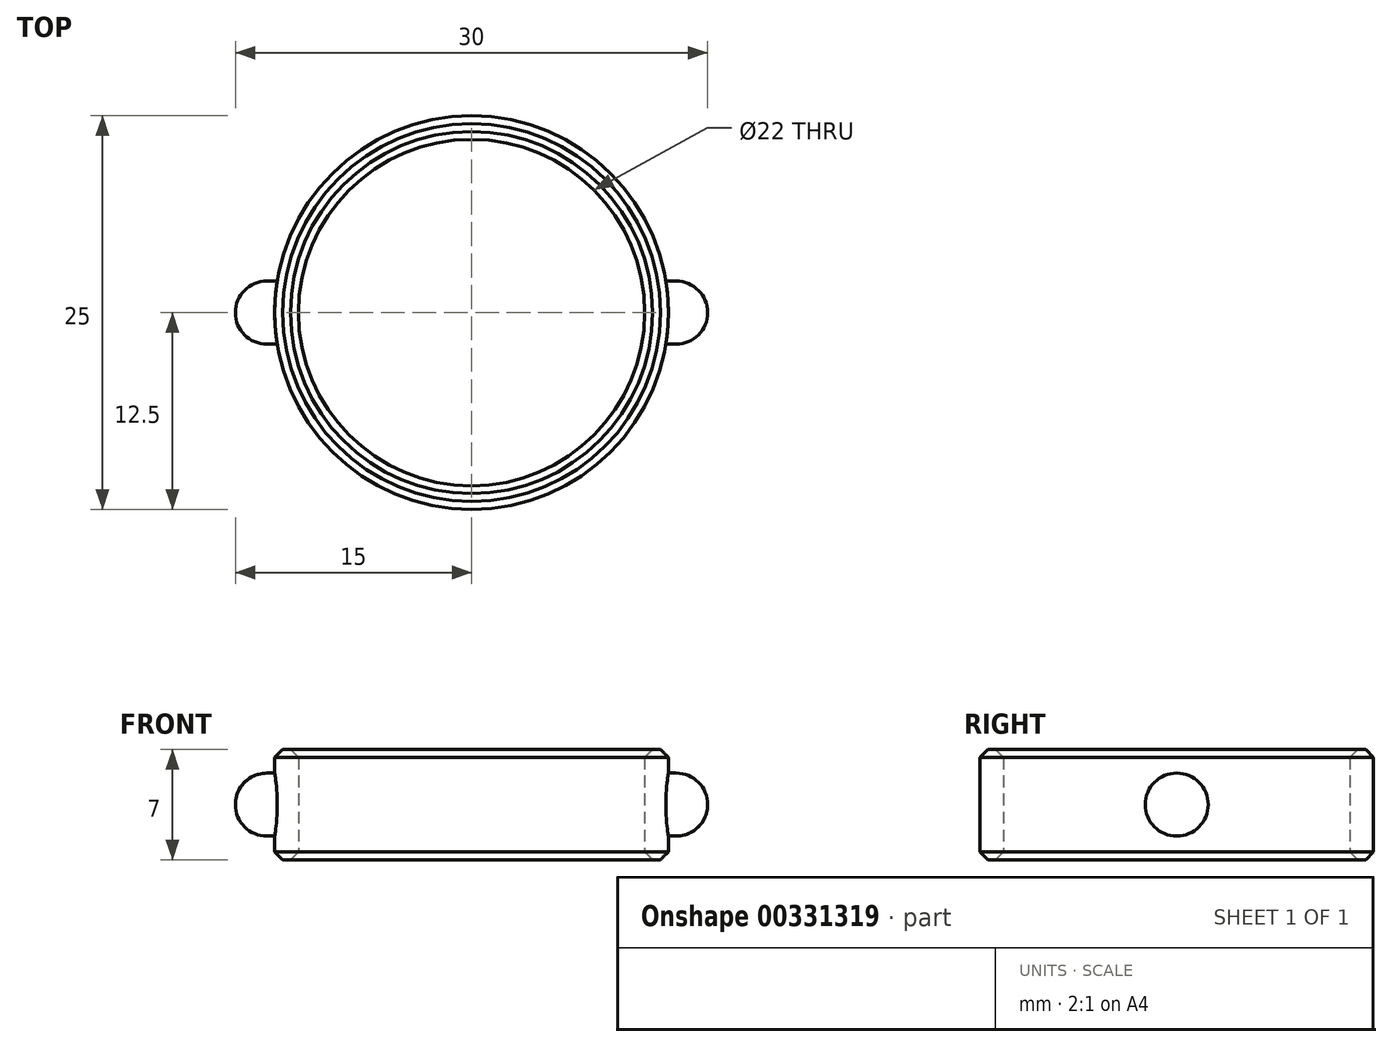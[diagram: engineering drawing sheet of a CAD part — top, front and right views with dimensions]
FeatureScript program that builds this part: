
annotation { "Feature Type Name" : "Feature", "Feature Type Description" : "" }
export const myFeature = defineFeature(function(context is Context, id is Id, definition is map)
    precondition{}
    {
        {
            var Q0;
            Q0=qCreatedBy(makeId("Top.planeOp"),FACE);
            var sketch = newSketch(context, id + "F0", { "sketchPlane" : qUnion([Q0])});
            skCircle(sketch, "E0", {"center": v(0, 0) * mm, "radius": 11 * mm});
            skCircle(sketch, "E1", {"center": v(0, 0) * mm, "radius": 12.5 * mm});
            skSolve(sketch);
        }
        {
            var Q0;
            Q0=makeQuery(id+"F0.imprint","IMPRINT",FACE,{"disambiguationData":[TD([[makeQuery(id+"F0.imprint","IMPRINT",EDGE,{"derivedFrom":sQuery(id+"F0.wireOp",EDGE,"E0")}),-1.0]])]});
            extrude(context, id + "F1", {"entities" : qUnion([Q0]), "depth" : 7 * mm});
        }
        {
            var Q0;
            Q0=makeQuery(id+"F1.opExtrude","CAP_EDGE",EDGE,{"disambiguationData":[OSD([sQuery(id+"F0.wireOp",EDGE,"E0")])],"isStart":false});
            var Q1;
            Q1=makeQuery(id+"F1.opExtrude","CAP_EDGE",EDGE,{"disambiguationData":[OSD([sQuery(id+"F0.wireOp",EDGE,"E1")])],"isStart":false});
            var Q2;
            Q2=makeQuery(id+"F1.opExtrude","CAP_EDGE",EDGE,{"disambiguationData":[OSD([sQuery(id+"F0.wireOp",EDGE,"E1")])],"isStart":true});
            var Q3;
            Q3=makeQuery(id+"F1.opExtrude","CAP_EDGE",EDGE,{"disambiguationData":[OSD([sQuery(id+"F0.wireOp",EDGE,"E0")])],"isStart":true});
            chamfer(context, id + "F2", {"entities" : qUnion([Q0, Q1, Q2, Q3]), "width" : .5 * mm, "tangentPropagation" : true});
        }
        {
            var Q0;
            Q0=qCreatedBy(makeId("Right.planeOp"),FACE);
            cPlane(context, id + "F3", {"entities" : qUnion([Q0]), "cplaneType" : CPlaneType.OFFSET, "offset" : 11 * mm, "width" : 150 * mm, "height" : 150 * mm});
        }
        {
            var Q0;
            Q0=qCreatedBy(id+"F3.planeOp",FACE);
            var sketch = newSketch(context, id + "F4", { "sketchPlane" : qUnion([Q0])});
            skCircle(sketch, "E2", {"center": v(0, 3.5) * mm, "radius": 2 * mm});
            skLineSegment(sketch, "E3", {"start": v(0, 3.5) * mm, "end": v(0, 7) * mm, "construction": true});
            skLineSegment(sketch, "E4", {"start": v(0, 3.5) * mm, "end": v(0, 0) * mm, "construction": true});
            skSolve(sketch);
        }
        {
            var Q0;
            Q0 = qSketchRegion(id + "F4", true);
            var Q1;
            Q1=sQuery(id+"F4.wireOp",EDGE,"E2");
            extrude(context, id + "F5", {"entities" : qUnion([Q0]), "operationType" : NewBodyOperationType.ADD, "surfaceEntities" : qUnion([Q1]), "depth" : 4 * mm});
        }
        {
            var Q0;
            Q0=makeQuery(id+"F1.opExtrude","SWEPT_BODY",BODY,{"disambiguationData":[OSD([sQuery(id+"F0.wireOp",EDGE,"E0"),sQuery(id+"F0.wireOp",EDGE,"E1")])]});
            var Q1;
            Q1=qCreatedBy(makeId("Right.planeOp"),FACE);
            mirror(context, id + "F6", {"operationType" : NewBodyOperationType.ADD, "entities" : qUnion([Q0]), "mirrorPlane" : qUnion([Q1])});
        }
        {
            var Q0;
            Q0=makeQuery(id+"F6.opPattern","COPY",EDGE,{"derivedFrom":makeQuery(id+"F5.opExtrude","CAP_EDGE",EDGE,{"disambiguationData":[OSD([sQuery(id+"F4.wireOp",EDGE,"E2")])],"isStart":false}),"instanceName":"1"});
            var Q1;
            Q1=makeQuery(id+"F5.opExtrude","CAP_EDGE",EDGE,{"disambiguationData":[OSD([sQuery(id+"F4.wireOp",EDGE,"E2")])],"isStart":false});
            fillet(context, id + "F7", {"entities" : qUnion([Q0, Q1]), "radius" : 2 * mm, "tangentPropagation" : true, "allowEdgeOverflow" : false});
        }
    });
